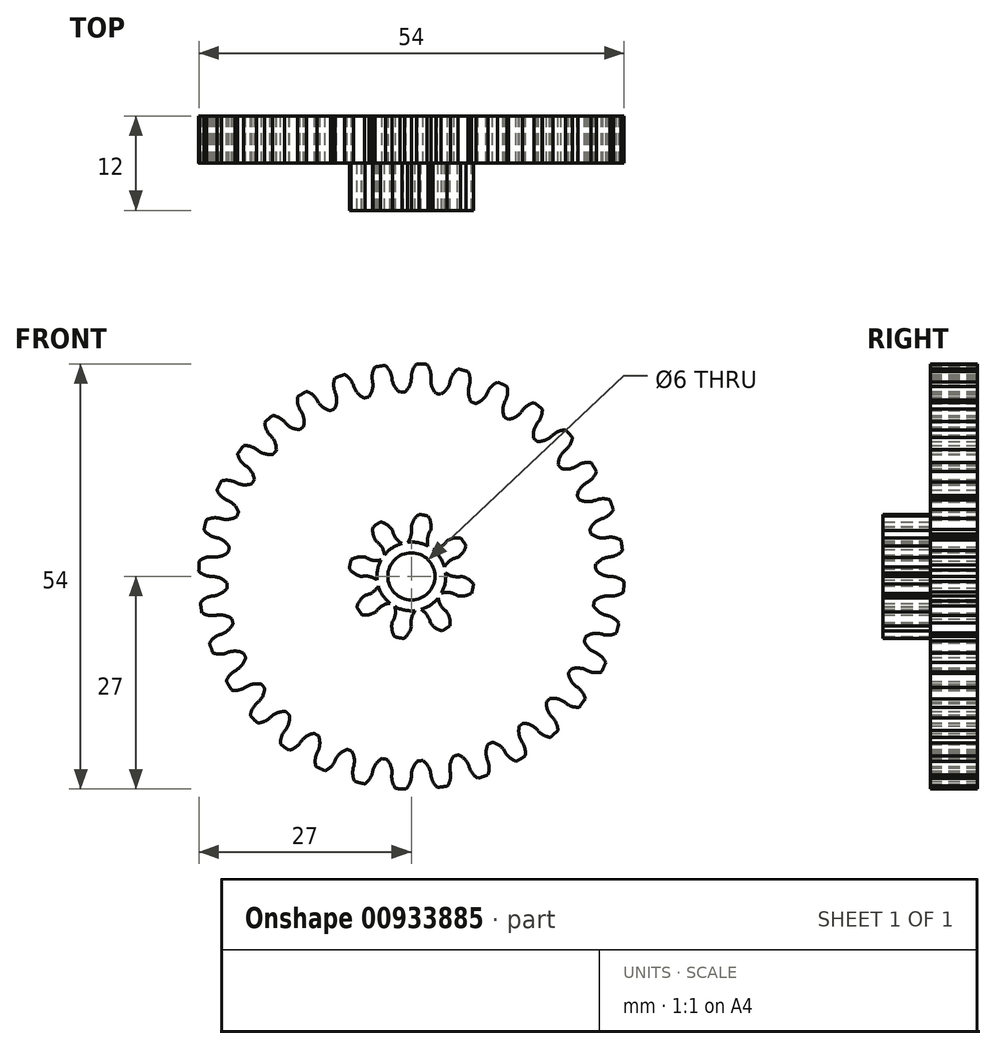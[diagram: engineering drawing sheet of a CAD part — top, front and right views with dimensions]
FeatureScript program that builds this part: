
annotation { "Feature Type Name" : "Feature", "Feature Type Description" : "" }
export const myFeature = defineFeature(function(context is Context, id is Id, definition is map)
    precondition{}
    {
        {
            var Q0;
            Q0=qCreatedBy(makeId("Front.planeOp"),FACE);
            var sketch = newSketch(context, id + "F0", { "sketchPlane" : qUnion([Q0])});
            skCircle(sketch, "E0", {"center": v(0, 0) * mm, "radius": 23.44 * mm});
            skArc(sketch, "E1", {"start": v(1.98, 26.94) * mm, "mid": v(1.33, 26.98) * mm, "end": v(0.67, 27) * mm});
            skArc(sketch, "E2", {"start": v(0.67, 27) * mm, "mid": v(0.2, 26.27) * mm, "end": v(0, 25.42) * mm});
            skArc(sketch, "E3", {"start": v(2.5, 25.3) * mm, "mid": v(2.58, 24.19) * mm, "end": v(3.14, 23.23) * mm});
            skArc(sketch, "E4", {"start": v(-0.85, 23.42) * mm, "mid": v(-0.2, 24.33) * mm, "end": v(0, 25.42) * mm});
            skArc(sketch, "E5.trimOffspring", {"start": v(2.5, 25.3) * mm, "mid": v(2.38, 26.17) * mm, "end": v(1.98, 26.94) * mm});
            skArc(sketch, "E6.1.0", {"start": v(-4.61, 26.62) * mm, "mid": v(-4.94, 25.8) * mm, "end": v(-4.96, 24.94) * mm});
            skArc(sketch, "E6.1.1", {"start": v(-2.49, 25.3) * mm, "mid": v(-2.19, 24.23) * mm, "end": v(-1.45, 23.4) * mm});
            skArc(sketch, "E6.1.2", {"start": v(-5.4, 22.8) * mm, "mid": v(-4.94, 23.82) * mm, "end": v(-4.96, 24.94) * mm});
            skArc(sketch, "E6.1.3", {"start": v(-2.49, 25.3) * mm, "mid": v(-2.77, 26.13) * mm, "end": v(-3.3, 26.8) * mm});
            skArc(sketch, "E6.1.4", {"start": v(-3.3, 26.8) * mm, "mid": v(-3.96, 26.72) * mm, "end": v(-4.61, 26.62) * mm});
            skArc(sketch, "E6.2.0", {"start": v(-9.72, 25.2) * mm, "mid": v(-9.88, 24.35) * mm, "end": v(-9.73, 23.49) * mm});
            skArc(sketch, "E6.2.1", {"start": v(-7.38, 24.33) * mm, "mid": v(-6.87, 23.34) * mm, "end": v(-5.98, 22.66) * mm});
            skArc(sketch, "E6.2.2", {"start": v(-9.75, 21.31) * mm, "mid": v(-9.49, 22.4) * mm, "end": v(-9.73, 23.49) * mm});
            skArc(sketch, "E6.2.3", {"start": v(-7.38, 24.33) * mm, "mid": v(-7.8, 25.09) * mm, "end": v(-8.48, 25.65) * mm});
            skArc(sketch, "E6.2.4", {"start": v(-8.48, 25.65) * mm, "mid": v(-9.1, 25.43) * mm, "end": v(-9.72, 25.2) * mm});
            skArc(sketch, "E6.3.0", {"start": v(-14.45, 22.82) * mm, "mid": v(-14.44, 21.95) * mm, "end": v(-14.12, 21.14) * mm});
            skArc(sketch, "E6.3.1", {"start": v(-11.98, 22.42) * mm, "mid": v(-11.3, 21.55) * mm, "end": v(-10.3, 21.06) * mm});
            skArc(sketch, "E6.3.2", {"start": v(-13.72, 19) * mm, "mid": v(-13.68, 20.12) * mm, "end": v(-14.12, 21.14) * mm});
            skArc(sketch, "E6.3.3", {"start": v(-11.98, 22.42) * mm, "mid": v(-12.55, 23.08) * mm, "end": v(-13.32, 23.5) * mm});
            skArc(sketch, "E6.3.4", {"start": v(-13.32, 23.5) * mm, "mid": v(-13.89, 23.17) * mm, "end": v(-14.45, 22.82) * mm});
            skArc(sketch, "E6.4.0", {"start": v(-18.62, 19.57) * mm, "mid": v(-18.44, 18.72) * mm, "end": v(-17.98, 17.98) * mm});
            skArc(sketch, "E6.4.1", {"start": v(-16.13, 19.65) * mm, "mid": v(-15.28, 18.93) * mm, "end": v(-14.2, 18.65) * mm});
            skArc(sketch, "E6.4.2", {"start": v(-17.16, 15.96) * mm, "mid": v(-17.34, 17.06) * mm, "end": v(-17.98, 17.98) * mm});
            skArc(sketch, "E6.4.3", {"start": v(-16.13, 19.65) * mm, "mid": v(-16.82, 20.19) * mm, "end": v(-17.65, 20.45) * mm});
            skArc(sketch, "E6.4.4", {"start": v(-17.65, 20.45) * mm, "mid": v(-18.14, 20.02) * mm, "end": v(-18.62, 19.57) * mm});
            skArc(sketch, "E6.5.0", {"start": v(-22.08, 15.56) * mm, "mid": v(-21.74, 14.76) * mm, "end": v(-21.14, 14.12) * mm});
            skArc(sketch, "E6.5.1", {"start": v(-19.65, 16.13) * mm, "mid": v(-18.68, 15.59) * mm, "end": v(-17.57, 15.52) * mm});
            skArc(sketch, "E6.5.2", {"start": v(-19.95, 12.3) * mm, "mid": v(-20.33, 13.35) * mm, "end": v(-21.14, 14.12) * mm});
            skArc(sketch, "E6.5.3", {"start": v(-19.65, 16.13) * mm, "mid": v(-20.43, 16.52) * mm, "end": v(-21.3, 16.62) * mm});
            skArc(sketch, "E6.5.4", {"start": v(-21.3, 16.62) * mm, "mid": v(-21.7, 16.1) * mm, "end": v(-22.08, 15.56) * mm});
            skArc(sketch, "E6.6.0", {"start": v(-24.7, 10.95) * mm, "mid": v(-24.2, 10.23) * mm, "end": v(-23.49, 9.73) * mm});
            skArc(sketch, "E6.6.1", {"start": v(-22.42, 11.99) * mm, "mid": v(-21.36, 11.64) * mm, "end": v(-20.26, 11.8) * mm});
            skArc(sketch, "E6.6.2", {"start": v(-21.96, 8.18) * mm, "mid": v(-22.55, 9.13) * mm, "end": v(-23.49, 9.73) * mm});
            skArc(sketch, "E6.6.3", {"start": v(-22.42, 11.99) * mm, "mid": v(-23.26, 12.22) * mm, "end": v(-24.13, 12.14) * mm});
            skArc(sketch, "E6.6.4", {"start": v(-24.13, 12.14) * mm, "mid": v(-24.42, 11.55) * mm, "end": v(-24.7, 10.95) * mm});
            skArc(sketch, "E6.7.0", {"start": v(-26.36, 5.92) * mm, "mid": v(-25.73, 5.32) * mm, "end": v(-24.94, 4.96) * mm});
            skArc(sketch, "E6.7.1", {"start": v(-24.33, 7.38) * mm, "mid": v(-23.22, 7.25) * mm, "end": v(-22.17, 7.61) * mm});
            skArc(sketch, "E6.7.2", {"start": v(-23.14, 3.74) * mm, "mid": v(-23.9, 4.55) * mm, "end": v(-24.94, 4.96) * mm});
            skArc(sketch, "E6.7.3", {"start": v(-24.33, 7.38) * mm, "mid": v(-25.2, 7.44) * mm, "end": v(-26.04, 7.2) * mm});
            skArc(sketch, "E6.7.4", {"start": v(-26.04, 7.2) * mm, "mid": v(-26.2, 6.56) * mm, "end": v(-26.36, 5.92) * mm});
            skArc(sketch, "E6.8.0", {"start": v(-27, 0.67) * mm, "mid": v(-26.27, 0.2) * mm, "end": v(-25.42, 0) * mm});
            skArc(sketch, "E6.8.1", {"start": v(-25.3, 2.5) * mm, "mid": v(-24.19, 2.58) * mm, "end": v(-23.23, 3.14) * mm});
            skArc(sketch, "E6.8.2", {"start": v(-23.42, -0.85) * mm, "mid": v(-24.33, -0.2) * mm, "end": v(-25.42, 0) * mm});
            skArc(sketch, "E6.8.3", {"start": v(-25.3, 2.5) * mm, "mid": v(-26.17, 2.38) * mm, "end": v(-26.94, 1.98) * mm});
            skArc(sketch, "E6.8.4", {"start": v(-26.94, 1.98) * mm, "mid": v(-26.98, 1.33) * mm, "end": v(-27, 0.67) * mm});
            skArc(sketch, "E6.9.0", {"start": v(-26.62, -4.61) * mm, "mid": v(-25.8, -4.94) * mm, "end": v(-24.94, -4.96) * mm});
            skArc(sketch, "E6.9.1", {"start": v(-25.3, -2.49) * mm, "mid": v(-24.23, -2.19) * mm, "end": v(-23.4, -1.45) * mm});
            skArc(sketch, "E6.9.2", {"start": v(-22.8, -5.4) * mm, "mid": v(-23.82, -4.94) * mm, "end": v(-24.94, -4.96) * mm});
            skArc(sketch, "E6.9.3", {"start": v(-25.3, -2.49) * mm, "mid": v(-26.13, -2.77) * mm, "end": v(-26.8, -3.3) * mm});
            skArc(sketch, "E6.9.4", {"start": v(-26.8, -3.3) * mm, "mid": v(-26.72, -3.96) * mm, "end": v(-26.62, -4.61) * mm});
            skArc(sketch, "E6.10.0", {"start": v(-25.2, -9.72) * mm, "mid": v(-24.35, -9.88) * mm, "end": v(-23.49, -9.73) * mm});
            skArc(sketch, "E6.10.1", {"start": v(-24.33, -7.38) * mm, "mid": v(-23.34, -6.87) * mm, "end": v(-22.66, -5.98) * mm});
            skArc(sketch, "E6.10.2", {"start": v(-21.31, -9.75) * mm, "mid": v(-22.4, -9.49) * mm, "end": v(-23.49, -9.73) * mm});
            skArc(sketch, "E6.10.3", {"start": v(-24.33, -7.38) * mm, "mid": v(-25.09, -7.8) * mm, "end": v(-25.65, -8.48) * mm});
            skArc(sketch, "E6.10.4", {"start": v(-25.65, -8.48) * mm, "mid": v(-25.43, -9.1) * mm, "end": v(-25.2, -9.72) * mm});
            skArc(sketch, "E6.11.0", {"start": v(-22.82, -14.45) * mm, "mid": v(-21.95, -14.44) * mm, "end": v(-21.14, -14.12) * mm});
            skArc(sketch, "E6.11.1", {"start": v(-22.42, -11.98) * mm, "mid": v(-21.55, -11.3) * mm, "end": v(-21.06, -10.3) * mm});
            skArc(sketch, "E6.11.2", {"start": v(-19, -13.72) * mm, "mid": v(-20.12, -13.68) * mm, "end": v(-21.14, -14.12) * mm});
            skArc(sketch, "E6.11.3", {"start": v(-22.42, -11.98) * mm, "mid": v(-23.08, -12.55) * mm, "end": v(-23.5, -13.32) * mm});
            skArc(sketch, "E6.11.4", {"start": v(-23.5, -13.32) * mm, "mid": v(-23.17, -13.89) * mm, "end": v(-22.82, -14.45) * mm});
            skArc(sketch, "E6.12.0", {"start": v(-19.57, -18.62) * mm, "mid": v(-18.72, -18.44) * mm, "end": v(-17.98, -17.98) * mm});
            skArc(sketch, "E6.12.1", {"start": v(-19.65, -16.13) * mm, "mid": v(-18.93, -15.28) * mm, "end": v(-18.65, -14.2) * mm});
            skArc(sketch, "E6.12.2", {"start": v(-15.96, -17.16) * mm, "mid": v(-17.06, -17.34) * mm, "end": v(-17.98, -17.98) * mm});
            skArc(sketch, "E6.12.3", {"start": v(-19.65, -16.13) * mm, "mid": v(-20.19, -16.82) * mm, "end": v(-20.45, -17.65) * mm});
            skArc(sketch, "E6.12.4", {"start": v(-20.45, -17.65) * mm, "mid": v(-20.02, -18.14) * mm, "end": v(-19.57, -18.62) * mm});
            skArc(sketch, "E6.13.0", {"start": v(-15.56, -22.08) * mm, "mid": v(-14.76, -21.74) * mm, "end": v(-14.12, -21.14) * mm});
            skArc(sketch, "E6.13.1", {"start": v(-16.13, -19.65) * mm, "mid": v(-15.59, -18.68) * mm, "end": v(-15.52, -17.57) * mm});
            skArc(sketch, "E6.13.2", {"start": v(-12.3, -19.95) * mm, "mid": v(-13.35, -20.33) * mm, "end": v(-14.12, -21.14) * mm});
            skArc(sketch, "E6.13.3", {"start": v(-16.13, -19.65) * mm, "mid": v(-16.52, -20.43) * mm, "end": v(-16.62, -21.3) * mm});
            skArc(sketch, "E6.13.4", {"start": v(-16.62, -21.3) * mm, "mid": v(-16.1, -21.7) * mm, "end": v(-15.56, -22.08) * mm});
            skArc(sketch, "E6.14.0", {"start": v(-10.95, -24.7) * mm, "mid": v(-10.23, -24.2) * mm, "end": v(-9.73, -23.49) * mm});
            skArc(sketch, "E6.14.1", {"start": v(-11.99, -22.42) * mm, "mid": v(-11.64, -21.36) * mm, "end": v(-11.8, -20.26) * mm});
            skArc(sketch, "E6.14.2", {"start": v(-8.18, -21.96) * mm, "mid": v(-9.13, -22.55) * mm, "end": v(-9.73, -23.49) * mm});
            skArc(sketch, "E6.14.3", {"start": v(-11.99, -22.42) * mm, "mid": v(-12.22, -23.26) * mm, "end": v(-12.14, -24.13) * mm});
            skArc(sketch, "E6.14.4", {"start": v(-12.14, -24.13) * mm, "mid": v(-11.55, -24.42) * mm, "end": v(-10.95, -24.7) * mm});
            skArc(sketch, "E6.15.0", {"start": v(-5.92, -26.36) * mm, "mid": v(-5.32, -25.73) * mm, "end": v(-4.96, -24.94) * mm});
            skArc(sketch, "E6.15.1", {"start": v(-7.38, -24.33) * mm, "mid": v(-7.25, -23.22) * mm, "end": v(-7.61, -22.17) * mm});
            skArc(sketch, "E6.15.2", {"start": v(-3.74, -23.14) * mm, "mid": v(-4.55, -23.9) * mm, "end": v(-4.96, -24.94) * mm});
            skArc(sketch, "E6.15.3", {"start": v(-7.38, -24.33) * mm, "mid": v(-7.44, -25.2) * mm, "end": v(-7.2, -26.04) * mm});
            skArc(sketch, "E6.15.4", {"start": v(-7.2, -26.04) * mm, "mid": v(-6.56, -26.2) * mm, "end": v(-5.92, -26.36) * mm});
            skArc(sketch, "E6.16.0", {"start": v(-0.67, -27) * mm, "mid": v(-0.2, -26.27) * mm, "end": v(0, -25.42) * mm});
            skArc(sketch, "E6.16.1", {"start": v(-2.5, -25.3) * mm, "mid": v(-2.58, -24.19) * mm, "end": v(-3.14, -23.23) * mm});
            skArc(sketch, "E6.16.2", {"start": v(0.85, -23.42) * mm, "mid": v(0.2, -24.33) * mm, "end": v(0, -25.42) * mm});
            skArc(sketch, "E6.16.3", {"start": v(-2.5, -25.3) * mm, "mid": v(-2.38, -26.17) * mm, "end": v(-1.98, -26.94) * mm});
            skArc(sketch, "E6.16.4", {"start": v(-1.98, -26.94) * mm, "mid": v(-1.33, -26.98) * mm, "end": v(-0.67, -27) * mm});
            skArc(sketch, "E6.17.0", {"start": v(4.61, -26.62) * mm, "mid": v(4.94, -25.8) * mm, "end": v(4.96, -24.94) * mm});
            skArc(sketch, "E6.17.1", {"start": v(2.49, -25.3) * mm, "mid": v(2.19, -24.23) * mm, "end": v(1.45, -23.4) * mm});
            skArc(sketch, "E6.17.2", {"start": v(5.4, -22.8) * mm, "mid": v(4.94, -23.82) * mm, "end": v(4.96, -24.94) * mm});
            skArc(sketch, "E6.17.3", {"start": v(2.49, -25.3) * mm, "mid": v(2.77, -26.13) * mm, "end": v(3.3, -26.8) * mm});
            skArc(sketch, "E6.17.4", {"start": v(3.3, -26.8) * mm, "mid": v(3.96, -26.72) * mm, "end": v(4.61, -26.62) * mm});
            skArc(sketch, "E6.18.0", {"start": v(9.72, -25.2) * mm, "mid": v(9.88, -24.35) * mm, "end": v(9.73, -23.49) * mm});
            skArc(sketch, "E6.18.1", {"start": v(7.38, -24.33) * mm, "mid": v(6.87, -23.34) * mm, "end": v(5.98, -22.66) * mm});
            skArc(sketch, "E6.18.2", {"start": v(9.75, -21.31) * mm, "mid": v(9.49, -22.4) * mm, "end": v(9.73, -23.49) * mm});
            skArc(sketch, "E6.18.3", {"start": v(7.38, -24.33) * mm, "mid": v(7.8, -25.09) * mm, "end": v(8.48, -25.65) * mm});
            skArc(sketch, "E6.18.4", {"start": v(8.48, -25.65) * mm, "mid": v(9.1, -25.43) * mm, "end": v(9.72, -25.2) * mm});
            skArc(sketch, "E6.19.0", {"start": v(14.45, -22.82) * mm, "mid": v(14.44, -21.95) * mm, "end": v(14.12, -21.14) * mm});
            skArc(sketch, "E6.19.1", {"start": v(11.98, -22.42) * mm, "mid": v(11.3, -21.55) * mm, "end": v(10.3, -21.06) * mm});
            skArc(sketch, "E6.19.2", {"start": v(13.72, -19) * mm, "mid": v(13.68, -20.12) * mm, "end": v(14.12, -21.14) * mm});
            skArc(sketch, "E6.19.3", {"start": v(11.98, -22.42) * mm, "mid": v(12.55, -23.08) * mm, "end": v(13.32, -23.5) * mm});
            skArc(sketch, "E6.19.4", {"start": v(13.32, -23.5) * mm, "mid": v(13.89, -23.17) * mm, "end": v(14.45, -22.82) * mm});
            skArc(sketch, "E6.20.0", {"start": v(18.62, -19.57) * mm, "mid": v(18.44, -18.72) * mm, "end": v(17.98, -17.98) * mm});
            skArc(sketch, "E6.20.1", {"start": v(16.13, -19.65) * mm, "mid": v(15.28, -18.93) * mm, "end": v(14.2, -18.65) * mm});
            skArc(sketch, "E6.20.2", {"start": v(17.16, -15.96) * mm, "mid": v(17.34, -17.06) * mm, "end": v(17.98, -17.98) * mm});
            skArc(sketch, "E6.20.3", {"start": v(16.13, -19.65) * mm, "mid": v(16.82, -20.19) * mm, "end": v(17.65, -20.45) * mm});
            skArc(sketch, "E6.20.4", {"start": v(17.65, -20.45) * mm, "mid": v(18.14, -20.02) * mm, "end": v(18.62, -19.57) * mm});
            skArc(sketch, "E6.21.0", {"start": v(22.08, -15.56) * mm, "mid": v(21.74, -14.76) * mm, "end": v(21.14, -14.12) * mm});
            skArc(sketch, "E6.21.1", {"start": v(19.65, -16.13) * mm, "mid": v(18.68, -15.59) * mm, "end": v(17.57, -15.52) * mm});
            skArc(sketch, "E6.21.2", {"start": v(19.95, -12.3) * mm, "mid": v(20.33, -13.35) * mm, "end": v(21.14, -14.12) * mm});
            skArc(sketch, "E6.21.3", {"start": v(19.65, -16.13) * mm, "mid": v(20.43, -16.52) * mm, "end": v(21.3, -16.62) * mm});
            skArc(sketch, "E6.21.4", {"start": v(21.3, -16.62) * mm, "mid": v(21.7, -16.1) * mm, "end": v(22.08, -15.56) * mm});
            skArc(sketch, "E6.22.0", {"start": v(24.7, -10.95) * mm, "mid": v(24.2, -10.23) * mm, "end": v(23.49, -9.73) * mm});
            skArc(sketch, "E6.22.1", {"start": v(22.42, -11.99) * mm, "mid": v(21.36, -11.64) * mm, "end": v(20.26, -11.8) * mm});
            skArc(sketch, "E6.22.2", {"start": v(21.96, -8.18) * mm, "mid": v(22.55, -9.13) * mm, "end": v(23.49, -9.73) * mm});
            skArc(sketch, "E6.22.3", {"start": v(22.42, -11.99) * mm, "mid": v(23.26, -12.22) * mm, "end": v(24.13, -12.14) * mm});
            skArc(sketch, "E6.22.4", {"start": v(24.13, -12.14) * mm, "mid": v(24.42, -11.55) * mm, "end": v(24.7, -10.95) * mm});
            skArc(sketch, "E6.23.0", {"start": v(26.36, -5.92) * mm, "mid": v(25.73, -5.32) * mm, "end": v(24.94, -4.96) * mm});
            skArc(sketch, "E6.23.1", {"start": v(24.33, -7.38) * mm, "mid": v(23.22, -7.25) * mm, "end": v(22.17, -7.61) * mm});
            skArc(sketch, "E6.23.2", {"start": v(23.14, -3.74) * mm, "mid": v(23.9, -4.55) * mm, "end": v(24.94, -4.96) * mm});
            skArc(sketch, "E6.23.3", {"start": v(24.33, -7.38) * mm, "mid": v(25.2, -7.44) * mm, "end": v(26.04, -7.2) * mm});
            skArc(sketch, "E6.23.4", {"start": v(26.04, -7.2) * mm, "mid": v(26.2, -6.56) * mm, "end": v(26.36, -5.92) * mm});
            skArc(sketch, "E6.24.0", {"start": v(27, -0.67) * mm, "mid": v(26.27, -0.2) * mm, "end": v(25.42, 0) * mm});
            skArc(sketch, "E6.24.1", {"start": v(25.3, -2.5) * mm, "mid": v(24.19, -2.58) * mm, "end": v(23.23, -3.14) * mm});
            skArc(sketch, "E6.24.2", {"start": v(23.42, 0.85) * mm, "mid": v(24.33, 0.2) * mm, "end": v(25.42, 0) * mm});
            skArc(sketch, "E6.24.3", {"start": v(25.3, -2.5) * mm, "mid": v(26.17, -2.38) * mm, "end": v(26.94, -1.98) * mm});
            skArc(sketch, "E6.24.4", {"start": v(26.94, -1.98) * mm, "mid": v(26.98, -1.33) * mm, "end": v(27, -0.67) * mm});
            skArc(sketch, "E6.25.0", {"start": v(26.62, 4.61) * mm, "mid": v(25.8, 4.94) * mm, "end": v(24.94, 4.96) * mm});
            skArc(sketch, "E6.25.1", {"start": v(25.3, 2.49) * mm, "mid": v(24.23, 2.19) * mm, "end": v(23.4, 1.45) * mm});
            skArc(sketch, "E6.25.2", {"start": v(22.8, 5.4) * mm, "mid": v(23.82, 4.94) * mm, "end": v(24.94, 4.96) * mm});
            skArc(sketch, "E6.25.3", {"start": v(25.3, 2.49) * mm, "mid": v(26.13, 2.77) * mm, "end": v(26.8, 3.3) * mm});
            skArc(sketch, "E6.25.4", {"start": v(26.8, 3.3) * mm, "mid": v(26.72, 3.96) * mm, "end": v(26.62, 4.61) * mm});
            skArc(sketch, "E6.26.0", {"start": v(25.2, 9.72) * mm, "mid": v(24.35, 9.88) * mm, "end": v(23.49, 9.73) * mm});
            skArc(sketch, "E6.26.1", {"start": v(24.33, 7.38) * mm, "mid": v(23.34, 6.87) * mm, "end": v(22.66, 5.98) * mm});
            skArc(sketch, "E6.26.2", {"start": v(21.31, 9.75) * mm, "mid": v(22.4, 9.49) * mm, "end": v(23.49, 9.73) * mm});
            skArc(sketch, "E6.26.3", {"start": v(24.33, 7.38) * mm, "mid": v(25.09, 7.8) * mm, "end": v(25.65, 8.48) * mm});
            skArc(sketch, "E6.26.4", {"start": v(25.65, 8.48) * mm, "mid": v(25.43, 9.1) * mm, "end": v(25.2, 9.72) * mm});
            skArc(sketch, "E6.27.0", {"start": v(22.82, 14.45) * mm, "mid": v(21.95, 14.44) * mm, "end": v(21.14, 14.12) * mm});
            skArc(sketch, "E6.27.1", {"start": v(22.42, 11.98) * mm, "mid": v(21.55, 11.3) * mm, "end": v(21.06, 10.3) * mm});
            skArc(sketch, "E6.27.2", {"start": v(19, 13.72) * mm, "mid": v(20.12, 13.68) * mm, "end": v(21.14, 14.12) * mm});
            skArc(sketch, "E6.27.3", {"start": v(22.42, 11.98) * mm, "mid": v(23.08, 12.55) * mm, "end": v(23.5, 13.32) * mm});
            skArc(sketch, "E6.27.4", {"start": v(23.5, 13.32) * mm, "mid": v(23.17, 13.89) * mm, "end": v(22.82, 14.45) * mm});
            skArc(sketch, "E6.28.0", {"start": v(19.57, 18.62) * mm, "mid": v(18.72, 18.44) * mm, "end": v(17.98, 17.98) * mm});
            skArc(sketch, "E6.28.1", {"start": v(19.65, 16.13) * mm, "mid": v(18.93, 15.28) * mm, "end": v(18.65, 14.2) * mm});
            skArc(sketch, "E6.28.2", {"start": v(15.96, 17.16) * mm, "mid": v(17.06, 17.34) * mm, "end": v(17.98, 17.98) * mm});
            skArc(sketch, "E6.28.3", {"start": v(19.65, 16.13) * mm, "mid": v(20.19, 16.82) * mm, "end": v(20.45, 17.65) * mm});
            skArc(sketch, "E6.28.4", {"start": v(20.45, 17.65) * mm, "mid": v(20.02, 18.14) * mm, "end": v(19.57, 18.62) * mm});
            skArc(sketch, "E6.29.0", {"start": v(15.56, 22.08) * mm, "mid": v(14.76, 21.74) * mm, "end": v(14.12, 21.14) * mm});
            skArc(sketch, "E6.29.1", {"start": v(16.13, 19.65) * mm, "mid": v(15.59, 18.68) * mm, "end": v(15.52, 17.57) * mm});
            skArc(sketch, "E6.29.2", {"start": v(12.3, 19.95) * mm, "mid": v(13.35, 20.33) * mm, "end": v(14.12, 21.14) * mm});
            skArc(sketch, "E6.29.3", {"start": v(16.13, 19.65) * mm, "mid": v(16.52, 20.43) * mm, "end": v(16.62, 21.3) * mm});
            skArc(sketch, "E6.29.4", {"start": v(16.62, 21.3) * mm, "mid": v(16.1, 21.7) * mm, "end": v(15.56, 22.08) * mm});
            skArc(sketch, "E6.30.0", {"start": v(10.95, 24.7) * mm, "mid": v(10.23, 24.2) * mm, "end": v(9.73, 23.49) * mm});
            skArc(sketch, "E6.30.1", {"start": v(11.99, 22.42) * mm, "mid": v(11.64, 21.36) * mm, "end": v(11.8, 20.26) * mm});
            skArc(sketch, "E6.30.2", {"start": v(8.18, 21.96) * mm, "mid": v(9.13, 22.55) * mm, "end": v(9.73, 23.49) * mm});
            skArc(sketch, "E6.30.3", {"start": v(11.99, 22.42) * mm, "mid": v(12.22, 23.26) * mm, "end": v(12.14, 24.13) * mm});
            skArc(sketch, "E6.30.4", {"start": v(12.14, 24.13) * mm, "mid": v(11.55, 24.42) * mm, "end": v(10.95, 24.7) * mm});
            skArc(sketch, "E6.31.0", {"start": v(5.92, 26.36) * mm, "mid": v(5.32, 25.73) * mm, "end": v(4.96, 24.94) * mm});
            skArc(sketch, "E6.31.1", {"start": v(7.38, 24.33) * mm, "mid": v(7.25, 23.22) * mm, "end": v(7.61, 22.17) * mm});
            skArc(sketch, "E6.31.2", {"start": v(3.74, 23.14) * mm, "mid": v(4.55, 23.9) * mm, "end": v(4.96, 24.94) * mm});
            skArc(sketch, "E6.31.3", {"start": v(7.38, 24.33) * mm, "mid": v(7.44, 25.2) * mm, "end": v(7.2, 26.04) * mm});
            skArc(sketch, "E6.31.4", {"start": v(7.2, 26.04) * mm, "mid": v(6.56, 26.2) * mm, "end": v(5.92, 26.36) * mm});
            skSolve(sketch);
        }
        {
            var Q0;
            Q0 = qSketchRegion(id + "F0", true);
            extrude(context, id + "F1", {"entities" : qUnion([Q0]), "depth" : 6 * mm, "offsetDistance" : 25 * mm});
        }
        {
            var Q0;
            Q0=makeQuery(id+"F1.opExtrude","CAP_FACE",FACE,{"disambiguationData":[OSD([sQuery(id+"F0.wireOp",EDGE,"E0"),sQuery(id+"F0.wireOp",EDGE,"E1"),sQuery(id+"F0.wireOp",EDGE,"E2"),sQuery(id+"F0.wireOp",EDGE,"E3"),sQuery(id+"F0.wireOp",EDGE,"E4"),sQuery(id+"F0.wireOp",EDGE,"E5.trimOffspring"),sQuery(id+"F0.wireOp",EDGE,"E6.1.0"),sQuery(id+"F0.wireOp",EDGE,"E6.1.1"),sQuery(id+"F0.wireOp",EDGE,"E6.1.2"),sQuery(id+"F0.wireOp",EDGE,"E6.1.3"),sQuery(id+"F0.wireOp",EDGE,"E6.1.4"),sQuery(id+"F0.wireOp",EDGE,"E6.2.0"),sQuery(id+"F0.wireOp",EDGE,"E6.2.1"),sQuery(id+"F0.wireOp",EDGE,"E6.2.2"),sQuery(id+"F0.wireOp",EDGE,"E6.2.3"),sQuery(id+"F0.wireOp",EDGE,"E6.2.4"),sQuery(id+"F0.wireOp",EDGE,"E6.3.0"),sQuery(id+"F0.wireOp",EDGE,"E6.3.1"),sQuery(id+"F0.wireOp",EDGE,"E6.3.2"),sQuery(id+"F0.wireOp",EDGE,"E6.3.3"),sQuery(id+"F0.wireOp",EDGE,"E6.3.4"),sQuery(id+"F0.wireOp",EDGE,"E6.4.0"),sQuery(id+"F0.wireOp",EDGE,"E6.4.1"),sQuery(id+"F0.wireOp",EDGE,"E6.4.2"),sQuery(id+"F0.wireOp",EDGE,"E6.4.3"),sQuery(id+"F0.wireOp",EDGE,"E6.4.4"),sQuery(id+"F0.wireOp",EDGE,"E6.5.0"),sQuery(id+"F0.wireOp",EDGE,"E6.5.1"),sQuery(id+"F0.wireOp",EDGE,"E6.5.2"),sQuery(id+"F0.wireOp",EDGE,"E6.5.3"),sQuery(id+"F0.wireOp",EDGE,"E6.5.4"),sQuery(id+"F0.wireOp",EDGE,"E6.6.0"),sQuery(id+"F0.wireOp",EDGE,"E6.6.1"),sQuery(id+"F0.wireOp",EDGE,"E6.6.2"),sQuery(id+"F0.wireOp",EDGE,"E6.6.3"),sQuery(id+"F0.wireOp",EDGE,"E6.6.4"),sQuery(id+"F0.wireOp",EDGE,"E6.7.0"),sQuery(id+"F0.wireOp",EDGE,"E6.7.1"),sQuery(id+"F0.wireOp",EDGE,"E6.7.2"),sQuery(id+"F0.wireOp",EDGE,"E6.7.3"),sQuery(id+"F0.wireOp",EDGE,"E6.7.4"),sQuery(id+"F0.wireOp",EDGE,"E6.8.0"),sQuery(id+"F0.wireOp",EDGE,"E6.8.1"),sQuery(id+"F0.wireOp",EDGE,"E6.8.2"),sQuery(id+"F0.wireOp",EDGE,"E6.8.3"),sQuery(id+"F0.wireOp",EDGE,"E6.8.4"),sQuery(id+"F0.wireOp",EDGE,"E6.9.0"),sQuery(id+"F0.wireOp",EDGE,"E6.9.1"),sQuery(id+"F0.wireOp",EDGE,"E6.9.2"),sQuery(id+"F0.wireOp",EDGE,"E6.9.3"),sQuery(id+"F0.wireOp",EDGE,"E6.9.4"),sQuery(id+"F0.wireOp",EDGE,"E6.10.0"),sQuery(id+"F0.wireOp",EDGE,"E6.10.1"),sQuery(id+"F0.wireOp",EDGE,"E6.10.2"),sQuery(id+"F0.wireOp",EDGE,"E6.10.3"),sQuery(id+"F0.wireOp",EDGE,"E6.10.4"),sQuery(id+"F0.wireOp",EDGE,"E6.11.0"),sQuery(id+"F0.wireOp",EDGE,"E6.11.1"),sQuery(id+"F0.wireOp",EDGE,"E6.11.2"),sQuery(id+"F0.wireOp",EDGE,"E6.11.3"),sQuery(id+"F0.wireOp",EDGE,"E6.11.4"),sQuery(id+"F0.wireOp",EDGE,"E6.12.0"),sQuery(id+"F0.wireOp",EDGE,"E6.12.1"),sQuery(id+"F0.wireOp",EDGE,"E6.12.2"),sQuery(id+"F0.wireOp",EDGE,"E6.12.3"),sQuery(id+"F0.wireOp",EDGE,"E6.12.4"),sQuery(id+"F0.wireOp",EDGE,"E6.13.0"),sQuery(id+"F0.wireOp",EDGE,"E6.13.1"),sQuery(id+"F0.wireOp",EDGE,"E6.13.2"),sQuery(id+"F0.wireOp",EDGE,"E6.13.3"),sQuery(id+"F0.wireOp",EDGE,"E6.13.4"),sQuery(id+"F0.wireOp",EDGE,"E6.14.0"),sQuery(id+"F0.wireOp",EDGE,"E6.14.1"),sQuery(id+"F0.wireOp",EDGE,"E6.14.2"),sQuery(id+"F0.wireOp",EDGE,"E6.14.3"),sQuery(id+"F0.wireOp",EDGE,"E6.14.4"),sQuery(id+"F0.wireOp",EDGE,"E6.15.0"),sQuery(id+"F0.wireOp",EDGE,"E6.15.1"),sQuery(id+"F0.wireOp",EDGE,"E6.15.2"),sQuery(id+"F0.wireOp",EDGE,"E6.15.3"),sQuery(id+"F0.wireOp",EDGE,"E6.15.4"),sQuery(id+"F0.wireOp",EDGE,"E6.16.0"),sQuery(id+"F0.wireOp",EDGE,"E6.16.1"),sQuery(id+"F0.wireOp",EDGE,"E6.16.2"),sQuery(id+"F0.wireOp",EDGE,"E6.16.3"),sQuery(id+"F0.wireOp",EDGE,"E6.16.4"),sQuery(id+"F0.wireOp",EDGE,"E6.17.0"),sQuery(id+"F0.wireOp",EDGE,"E6.17.1"),sQuery(id+"F0.wireOp",EDGE,"E6.17.2"),sQuery(id+"F0.wireOp",EDGE,"E6.17.3"),sQuery(id+"F0.wireOp",EDGE,"E6.17.4"),sQuery(id+"F0.wireOp",EDGE,"E6.18.0"),sQuery(id+"F0.wireOp",EDGE,"E6.18.1"),sQuery(id+"F0.wireOp",EDGE,"E6.18.2"),sQuery(id+"F0.wireOp",EDGE,"E6.18.3"),sQuery(id+"F0.wireOp",EDGE,"E6.18.4"),sQuery(id+"F0.wireOp",EDGE,"E6.19.0"),sQuery(id+"F0.wireOp",EDGE,"E6.19.1"),sQuery(id+"F0.wireOp",EDGE,"E6.19.2"),sQuery(id+"F0.wireOp",EDGE,"E6.19.3"),sQuery(id+"F0.wireOp",EDGE,"E6.19.4"),sQuery(id+"F0.wireOp",EDGE,"E6.20.0"),sQuery(id+"F0.wireOp",EDGE,"E6.20.1"),sQuery(id+"F0.wireOp",EDGE,"E6.20.2"),sQuery(id+"F0.wireOp",EDGE,"E6.20.3"),sQuery(id+"F0.wireOp",EDGE,"E6.20.4"),sQuery(id+"F0.wireOp",EDGE,"E6.21.0"),sQuery(id+"F0.wireOp",EDGE,"E6.21.1"),sQuery(id+"F0.wireOp",EDGE,"E6.21.2"),sQuery(id+"F0.wireOp",EDGE,"E6.21.3"),sQuery(id+"F0.wireOp",EDGE,"E6.21.4"),sQuery(id+"F0.wireOp",EDGE,"E6.22.0"),sQuery(id+"F0.wireOp",EDGE,"E6.22.1"),sQuery(id+"F0.wireOp",EDGE,"E6.22.2"),sQuery(id+"F0.wireOp",EDGE,"E6.22.3"),sQuery(id+"F0.wireOp",EDGE,"E6.22.4"),sQuery(id+"F0.wireOp",EDGE,"E6.23.0"),sQuery(id+"F0.wireOp",EDGE,"E6.23.1"),sQuery(id+"F0.wireOp",EDGE,"E6.23.2"),sQuery(id+"F0.wireOp",EDGE,"E6.23.3"),sQuery(id+"F0.wireOp",EDGE,"E6.23.4"),sQuery(id+"F0.wireOp",EDGE,"E6.24.0"),sQuery(id+"F0.wireOp",EDGE,"E6.24.1"),sQuery(id+"F0.wireOp",EDGE,"E6.24.2"),sQuery(id+"F0.wireOp",EDGE,"E6.24.3"),sQuery(id+"F0.wireOp",EDGE,"E6.24.4"),sQuery(id+"F0.wireOp",EDGE,"E6.25.0"),sQuery(id+"F0.wireOp",EDGE,"E6.25.1"),sQuery(id+"F0.wireOp",EDGE,"E6.25.2"),sQuery(id+"F0.wireOp",EDGE,"E6.25.3"),sQuery(id+"F0.wireOp",EDGE,"E6.25.4"),sQuery(id+"F0.wireOp",EDGE,"E6.26.0"),sQuery(id+"F0.wireOp",EDGE,"E6.26.1"),sQuery(id+"F0.wireOp",EDGE,"E6.26.2"),sQuery(id+"F0.wireOp",EDGE,"E6.26.3"),sQuery(id+"F0.wireOp",EDGE,"E6.26.4"),sQuery(id+"F0.wireOp",EDGE,"E6.27.0"),sQuery(id+"F0.wireOp",EDGE,"E6.27.1"),sQuery(id+"F0.wireOp",EDGE,"E6.27.2"),sQuery(id+"F0.wireOp",EDGE,"E6.27.3"),sQuery(id+"F0.wireOp",EDGE,"E6.27.4"),sQuery(id+"F0.wireOp",EDGE,"E6.28.0"),sQuery(id+"F0.wireOp",EDGE,"E6.28.1"),sQuery(id+"F0.wireOp",EDGE,"E6.28.2"),sQuery(id+"F0.wireOp",EDGE,"E6.28.3"),sQuery(id+"F0.wireOp",EDGE,"E6.28.4"),sQuery(id+"F0.wireOp",EDGE,"E6.29.0"),sQuery(id+"F0.wireOp",EDGE,"E6.29.1"),sQuery(id+"F0.wireOp",EDGE,"E6.29.2"),sQuery(id+"F0.wireOp",EDGE,"E6.29.3"),sQuery(id+"F0.wireOp",EDGE,"E6.29.4"),sQuery(id+"F0.wireOp",EDGE,"E6.30.0"),sQuery(id+"F0.wireOp",EDGE,"E6.30.1"),sQuery(id+"F0.wireOp",EDGE,"E6.30.2"),sQuery(id+"F0.wireOp",EDGE,"E6.30.3"),sQuery(id+"F0.wireOp",EDGE,"E6.30.4"),sQuery(id+"F0.wireOp",EDGE,"E6.31.0"),sQuery(id+"F0.wireOp",EDGE,"E6.31.1"),sQuery(id+"F0.wireOp",EDGE,"E6.31.2"),sQuery(id+"F0.wireOp",EDGE,"E6.31.3"),sQuery(id+"F0.wireOp",EDGE,"E6.31.4")])],"isStart":false});
            var sketch = newSketch(context, id + "F2", { "sketchPlane" : qUnion([Q0])});
            skCircle(sketch, "E7", {"center": v(0, 0) * mm, "radius": 3 * mm});
            skSolve(sketch);
        }
        {
            var Q0;
            Q0 = qSketchRegion(id + "F2", true);
            extrude(context, id + "F3", {"entities" : qUnion([Q0]), "operationType" : NewBodyOperationType.REMOVE, "endBound" : BoundingType.THROUGH_ALL, "oppositeDirection" : true, "depth" : 25 * mm, "offsetDistance" : 25 * mm});
        }
        {
            var Q0;
            Q0=makeQuery(id+"F1.opExtrude","CAP_FACE",FACE,{"disambiguationData":[OSD([sQuery(id+"F0.wireOp",EDGE,"E0"),sQuery(id+"F0.wireOp",EDGE,"E1"),sQuery(id+"F0.wireOp",EDGE,"E2"),sQuery(id+"F0.wireOp",EDGE,"E3"),sQuery(id+"F0.wireOp",EDGE,"E4"),sQuery(id+"F0.wireOp",EDGE,"E5.trimOffspring"),sQuery(id+"F0.wireOp",EDGE,"E6.1.0"),sQuery(id+"F0.wireOp",EDGE,"E6.1.1"),sQuery(id+"F0.wireOp",EDGE,"E6.1.2"),sQuery(id+"F0.wireOp",EDGE,"E6.1.3"),sQuery(id+"F0.wireOp",EDGE,"E6.1.4"),sQuery(id+"F0.wireOp",EDGE,"E6.2.0"),sQuery(id+"F0.wireOp",EDGE,"E6.2.1"),sQuery(id+"F0.wireOp",EDGE,"E6.2.2"),sQuery(id+"F0.wireOp",EDGE,"E6.2.3"),sQuery(id+"F0.wireOp",EDGE,"E6.2.4"),sQuery(id+"F0.wireOp",EDGE,"E6.3.0"),sQuery(id+"F0.wireOp",EDGE,"E6.3.1"),sQuery(id+"F0.wireOp",EDGE,"E6.3.2"),sQuery(id+"F0.wireOp",EDGE,"E6.3.3"),sQuery(id+"F0.wireOp",EDGE,"E6.3.4"),sQuery(id+"F0.wireOp",EDGE,"E6.4.0"),sQuery(id+"F0.wireOp",EDGE,"E6.4.1"),sQuery(id+"F0.wireOp",EDGE,"E6.4.2"),sQuery(id+"F0.wireOp",EDGE,"E6.4.3"),sQuery(id+"F0.wireOp",EDGE,"E6.4.4"),sQuery(id+"F0.wireOp",EDGE,"E6.5.0"),sQuery(id+"F0.wireOp",EDGE,"E6.5.1"),sQuery(id+"F0.wireOp",EDGE,"E6.5.2"),sQuery(id+"F0.wireOp",EDGE,"E6.5.3"),sQuery(id+"F0.wireOp",EDGE,"E6.5.4"),sQuery(id+"F0.wireOp",EDGE,"E6.6.0"),sQuery(id+"F0.wireOp",EDGE,"E6.6.1"),sQuery(id+"F0.wireOp",EDGE,"E6.6.2"),sQuery(id+"F0.wireOp",EDGE,"E6.6.3"),sQuery(id+"F0.wireOp",EDGE,"E6.6.4"),sQuery(id+"F0.wireOp",EDGE,"E6.7.0"),sQuery(id+"F0.wireOp",EDGE,"E6.7.1"),sQuery(id+"F0.wireOp",EDGE,"E6.7.2"),sQuery(id+"F0.wireOp",EDGE,"E6.7.3"),sQuery(id+"F0.wireOp",EDGE,"E6.7.4"),sQuery(id+"F0.wireOp",EDGE,"E6.8.0"),sQuery(id+"F0.wireOp",EDGE,"E6.8.1"),sQuery(id+"F0.wireOp",EDGE,"E6.8.2"),sQuery(id+"F0.wireOp",EDGE,"E6.8.3"),sQuery(id+"F0.wireOp",EDGE,"E6.8.4"),sQuery(id+"F0.wireOp",EDGE,"E6.9.0"),sQuery(id+"F0.wireOp",EDGE,"E6.9.1"),sQuery(id+"F0.wireOp",EDGE,"E6.9.2"),sQuery(id+"F0.wireOp",EDGE,"E6.9.3"),sQuery(id+"F0.wireOp",EDGE,"E6.9.4"),sQuery(id+"F0.wireOp",EDGE,"E6.10.0"),sQuery(id+"F0.wireOp",EDGE,"E6.10.1"),sQuery(id+"F0.wireOp",EDGE,"E6.10.2"),sQuery(id+"F0.wireOp",EDGE,"E6.10.3"),sQuery(id+"F0.wireOp",EDGE,"E6.10.4"),sQuery(id+"F0.wireOp",EDGE,"E6.11.0"),sQuery(id+"F0.wireOp",EDGE,"E6.11.1"),sQuery(id+"F0.wireOp",EDGE,"E6.11.2"),sQuery(id+"F0.wireOp",EDGE,"E6.11.3"),sQuery(id+"F0.wireOp",EDGE,"E6.11.4"),sQuery(id+"F0.wireOp",EDGE,"E6.12.0"),sQuery(id+"F0.wireOp",EDGE,"E6.12.1"),sQuery(id+"F0.wireOp",EDGE,"E6.12.2"),sQuery(id+"F0.wireOp",EDGE,"E6.12.3"),sQuery(id+"F0.wireOp",EDGE,"E6.12.4"),sQuery(id+"F0.wireOp",EDGE,"E6.13.0"),sQuery(id+"F0.wireOp",EDGE,"E6.13.1"),sQuery(id+"F0.wireOp",EDGE,"E6.13.2"),sQuery(id+"F0.wireOp",EDGE,"E6.13.3"),sQuery(id+"F0.wireOp",EDGE,"E6.13.4"),sQuery(id+"F0.wireOp",EDGE,"E6.14.0"),sQuery(id+"F0.wireOp",EDGE,"E6.14.1"),sQuery(id+"F0.wireOp",EDGE,"E6.14.2"),sQuery(id+"F0.wireOp",EDGE,"E6.14.3"),sQuery(id+"F0.wireOp",EDGE,"E6.14.4"),sQuery(id+"F0.wireOp",EDGE,"E6.15.0"),sQuery(id+"F0.wireOp",EDGE,"E6.15.1"),sQuery(id+"F0.wireOp",EDGE,"E6.15.2"),sQuery(id+"F0.wireOp",EDGE,"E6.15.3"),sQuery(id+"F0.wireOp",EDGE,"E6.15.4"),sQuery(id+"F0.wireOp",EDGE,"E6.16.0"),sQuery(id+"F0.wireOp",EDGE,"E6.16.1"),sQuery(id+"F0.wireOp",EDGE,"E6.16.2"),sQuery(id+"F0.wireOp",EDGE,"E6.16.3"),sQuery(id+"F0.wireOp",EDGE,"E6.16.4"),sQuery(id+"F0.wireOp",EDGE,"E6.17.0"),sQuery(id+"F0.wireOp",EDGE,"E6.17.1"),sQuery(id+"F0.wireOp",EDGE,"E6.17.2"),sQuery(id+"F0.wireOp",EDGE,"E6.17.3"),sQuery(id+"F0.wireOp",EDGE,"E6.17.4"),sQuery(id+"F0.wireOp",EDGE,"E6.18.0"),sQuery(id+"F0.wireOp",EDGE,"E6.18.1"),sQuery(id+"F0.wireOp",EDGE,"E6.18.2"),sQuery(id+"F0.wireOp",EDGE,"E6.18.3"),sQuery(id+"F0.wireOp",EDGE,"E6.18.4"),sQuery(id+"F0.wireOp",EDGE,"E6.19.0"),sQuery(id+"F0.wireOp",EDGE,"E6.19.1"),sQuery(id+"F0.wireOp",EDGE,"E6.19.2"),sQuery(id+"F0.wireOp",EDGE,"E6.19.3"),sQuery(id+"F0.wireOp",EDGE,"E6.19.4"),sQuery(id+"F0.wireOp",EDGE,"E6.20.0"),sQuery(id+"F0.wireOp",EDGE,"E6.20.1"),sQuery(id+"F0.wireOp",EDGE,"E6.20.2"),sQuery(id+"F0.wireOp",EDGE,"E6.20.3"),sQuery(id+"F0.wireOp",EDGE,"E6.20.4"),sQuery(id+"F0.wireOp",EDGE,"E6.21.0"),sQuery(id+"F0.wireOp",EDGE,"E6.21.1"),sQuery(id+"F0.wireOp",EDGE,"E6.21.2"),sQuery(id+"F0.wireOp",EDGE,"E6.21.3"),sQuery(id+"F0.wireOp",EDGE,"E6.21.4"),sQuery(id+"F0.wireOp",EDGE,"E6.22.0"),sQuery(id+"F0.wireOp",EDGE,"E6.22.1"),sQuery(id+"F0.wireOp",EDGE,"E6.22.2"),sQuery(id+"F0.wireOp",EDGE,"E6.22.3"),sQuery(id+"F0.wireOp",EDGE,"E6.22.4"),sQuery(id+"F0.wireOp",EDGE,"E6.23.0"),sQuery(id+"F0.wireOp",EDGE,"E6.23.1"),sQuery(id+"F0.wireOp",EDGE,"E6.23.2"),sQuery(id+"F0.wireOp",EDGE,"E6.23.3"),sQuery(id+"F0.wireOp",EDGE,"E6.23.4"),sQuery(id+"F0.wireOp",EDGE,"E6.24.0"),sQuery(id+"F0.wireOp",EDGE,"E6.24.1"),sQuery(id+"F0.wireOp",EDGE,"E6.24.2"),sQuery(id+"F0.wireOp",EDGE,"E6.24.3"),sQuery(id+"F0.wireOp",EDGE,"E6.24.4"),sQuery(id+"F0.wireOp",EDGE,"E6.25.0"),sQuery(id+"F0.wireOp",EDGE,"E6.25.1"),sQuery(id+"F0.wireOp",EDGE,"E6.25.2"),sQuery(id+"F0.wireOp",EDGE,"E6.25.3"),sQuery(id+"F0.wireOp",EDGE,"E6.25.4"),sQuery(id+"F0.wireOp",EDGE,"E6.26.0"),sQuery(id+"F0.wireOp",EDGE,"E6.26.1"),sQuery(id+"F0.wireOp",EDGE,"E6.26.2"),sQuery(id+"F0.wireOp",EDGE,"E6.26.3"),sQuery(id+"F0.wireOp",EDGE,"E6.26.4"),sQuery(id+"F0.wireOp",EDGE,"E6.27.0"),sQuery(id+"F0.wireOp",EDGE,"E6.27.1"),sQuery(id+"F0.wireOp",EDGE,"E6.27.2"),sQuery(id+"F0.wireOp",EDGE,"E6.27.3"),sQuery(id+"F0.wireOp",EDGE,"E6.27.4"),sQuery(id+"F0.wireOp",EDGE,"E6.28.0"),sQuery(id+"F0.wireOp",EDGE,"E6.28.1"),sQuery(id+"F0.wireOp",EDGE,"E6.28.2"),sQuery(id+"F0.wireOp",EDGE,"E6.28.3"),sQuery(id+"F0.wireOp",EDGE,"E6.28.4"),sQuery(id+"F0.wireOp",EDGE,"E6.29.0"),sQuery(id+"F0.wireOp",EDGE,"E6.29.1"),sQuery(id+"F0.wireOp",EDGE,"E6.29.2"),sQuery(id+"F0.wireOp",EDGE,"E6.29.3"),sQuery(id+"F0.wireOp",EDGE,"E6.29.4"),sQuery(id+"F0.wireOp",EDGE,"E6.30.0"),sQuery(id+"F0.wireOp",EDGE,"E6.30.1"),sQuery(id+"F0.wireOp",EDGE,"E6.30.2"),sQuery(id+"F0.wireOp",EDGE,"E6.30.3"),sQuery(id+"F0.wireOp",EDGE,"E6.30.4"),sQuery(id+"F0.wireOp",EDGE,"E6.31.0"),sQuery(id+"F0.wireOp",EDGE,"E6.31.1"),sQuery(id+"F0.wireOp",EDGE,"E6.31.2"),sQuery(id+"F0.wireOp",EDGE,"E6.31.3"),sQuery(id+"F0.wireOp",EDGE,"E6.31.4")])],"isStart":false});
            var sketch = newSketch(context, id + "F4", { "sketchPlane" : qUnion([Q0])});
            skCircle(sketch, "E8", {"center": v(0, 0) * mm, "radius": 4.37 * mm});
            skArc(sketch, "E9", {"start": v(2.13, 7.65) * mm, "mid": v(1.56, 7.8) * mm, "end": v(0.98, 7.88) * mm});
            skArc(sketch, "E10", {"start": v(2.45, 5.87) * mm, "mid": v(2.06, 4.88) * mm, "end": v(2.1, 3.83) * mm});
            skArc(sketch, "E11", {"start": v(-0.47, 4.34) * mm, "mid": v(-0.02, 5.3) * mm, "end": v(0, 6.36) * mm});
            skArc(sketch, "E12.trimOffspring", {"start": v(2.45, 5.87) * mm, "mid": v(2.46, 6.79) * mm, "end": v(2.13, 7.65) * mm});
            skArc(sketch, "E13.trimOffspring", {"start": v(0.98, 7.88) * mm, "mid": v(0.35, 7.21) * mm, "end": v(0, 6.36) * mm});
            skArc(sketch, "E14.1.0", {"start": v(-3.9, 6.92) * mm, "mid": v(-4.4, 6.61) * mm, "end": v(-4.88, 6.27) * mm});
            skArc(sketch, "E14.1.1", {"start": v(-4.88, 6.27) * mm, "mid": v(-4.86, 5.34) * mm, "end": v(-4.5, 4.5) * mm});
            skArc(sketch, "E14.1.2", {"start": v(-2.42, 5.88) * mm, "mid": v(-3.06, 6.54) * mm, "end": v(-3.9, 6.92) * mm});
            skArc(sketch, "E14.1.3", {"start": v(-2.42, 5.88) * mm, "mid": v(-2, 4.9) * mm, "end": v(-1.22, 4.2) * mm});
            skArc(sketch, "E14.1.4", {"start": v(-3.4, 2.74) * mm, "mid": v(-3.76, 3.74) * mm, "end": v(-4.5, 4.5) * mm});
            skArc(sketch, "E14.2.0", {"start": v(-7.65, 2.13) * mm, "mid": v(-7.8, 1.56) * mm, "end": v(-7.88, 0.98) * mm});
            skArc(sketch, "E14.2.1", {"start": v(-7.88, 0.98) * mm, "mid": v(-7.21, 0.35) * mm, "end": v(-6.36, 0) * mm});
            skArc(sketch, "E14.2.2", {"start": v(-5.87, 2.45) * mm, "mid": v(-6.79, 2.46) * mm, "end": v(-7.65, 2.13) * mm});
            skArc(sketch, "E14.2.3", {"start": v(-5.87, 2.45) * mm, "mid": v(-4.88, 2.06) * mm, "end": v(-3.83, 2.1) * mm});
            skArc(sketch, "E14.2.4", {"start": v(-4.34, -0.47) * mm, "mid": v(-5.3, -0.02) * mm, "end": v(-6.36, 0) * mm});
            skArc(sketch, "E14.3.0", {"start": v(-6.92, -3.9) * mm, "mid": v(-6.61, -4.4) * mm, "end": v(-6.27, -4.88) * mm});
            skArc(sketch, "E14.3.1", {"start": v(-6.27, -4.88) * mm, "mid": v(-5.34, -4.86) * mm, "end": v(-4.5, -4.5) * mm});
            skArc(sketch, "E14.3.2", {"start": v(-5.88, -2.42) * mm, "mid": v(-6.54, -3.06) * mm, "end": v(-6.92, -3.9) * mm});
            skArc(sketch, "E14.3.3", {"start": v(-5.88, -2.42) * mm, "mid": v(-4.9, -2) * mm, "end": v(-4.2, -1.22) * mm});
            skArc(sketch, "E14.3.4", {"start": v(-2.74, -3.4) * mm, "mid": v(-3.74, -3.76) * mm, "end": v(-4.5, -4.5) * mm});
            skArc(sketch, "E14.4.0", {"start": v(-2.13, -7.65) * mm, "mid": v(-1.56, -7.8) * mm, "end": v(-0.98, -7.88) * mm});
            skArc(sketch, "E14.4.1", {"start": v(-0.98, -7.88) * mm, "mid": v(-0.35, -7.21) * mm, "end": v(0, -6.36) * mm});
            skArc(sketch, "E14.4.2", {"start": v(-2.45, -5.87) * mm, "mid": v(-2.46, -6.79) * mm, "end": v(-2.13, -7.65) * mm});
            skArc(sketch, "E14.4.3", {"start": v(-2.45, -5.87) * mm, "mid": v(-2.06, -4.88) * mm, "end": v(-2.1, -3.83) * mm});
            skArc(sketch, "E14.4.4", {"start": v(0.47, -4.34) * mm, "mid": v(0.02, -5.3) * mm, "end": v(0, -6.36) * mm});
            skArc(sketch, "E14.5.0", {"start": v(3.9, -6.92) * mm, "mid": v(4.4, -6.61) * mm, "end": v(4.88, -6.27) * mm});
            skArc(sketch, "E14.5.1", {"start": v(4.88, -6.27) * mm, "mid": v(4.86, -5.34) * mm, "end": v(4.5, -4.5) * mm});
            skArc(sketch, "E14.5.2", {"start": v(2.42, -5.88) * mm, "mid": v(3.06, -6.54) * mm, "end": v(3.9, -6.92) * mm});
            skArc(sketch, "E14.5.3", {"start": v(2.42, -5.88) * mm, "mid": v(2, -4.9) * mm, "end": v(1.22, -4.2) * mm});
            skArc(sketch, "E14.5.4", {"start": v(3.4, -2.74) * mm, "mid": v(3.76, -3.74) * mm, "end": v(4.5, -4.5) * mm});
            skArc(sketch, "E14.6.0", {"start": v(7.65, -2.13) * mm, "mid": v(7.8, -1.56) * mm, "end": v(7.88, -0.98) * mm});
            skArc(sketch, "E14.6.1", {"start": v(7.88, -0.98) * mm, "mid": v(7.21, -0.35) * mm, "end": v(6.36, 0) * mm});
            skArc(sketch, "E14.6.2", {"start": v(5.87, -2.45) * mm, "mid": v(6.79, -2.46) * mm, "end": v(7.65, -2.13) * mm});
            skArc(sketch, "E14.6.3", {"start": v(5.87, -2.45) * mm, "mid": v(4.88, -2.06) * mm, "end": v(3.83, -2.1) * mm});
            skArc(sketch, "E14.6.4", {"start": v(4.34, 0.47) * mm, "mid": v(5.3, 0.02) * mm, "end": v(6.36, 0) * mm});
            skArc(sketch, "E14.7.0", {"start": v(6.92, 3.9) * mm, "mid": v(6.61, 4.4) * mm, "end": v(6.27, 4.88) * mm});
            skArc(sketch, "E14.7.1", {"start": v(6.27, 4.88) * mm, "mid": v(5.34, 4.86) * mm, "end": v(4.5, 4.5) * mm});
            skArc(sketch, "E14.7.2", {"start": v(5.88, 2.42) * mm, "mid": v(6.54, 3.06) * mm, "end": v(6.92, 3.9) * mm});
            skArc(sketch, "E14.7.3", {"start": v(5.88, 2.42) * mm, "mid": v(4.9, 2) * mm, "end": v(4.2, 1.22) * mm});
            skArc(sketch, "E14.7.4", {"start": v(2.74, 3.4) * mm, "mid": v(3.74, 3.76) * mm, "end": v(4.5, 4.5) * mm});
            skSolve(sketch);
        }
        {
            var Q0;
            Q0=makeQuery(id+"F4.imprint","IMPRINT",FACE,{"disambiguationData":[TD([[makeQuery(id+"F4.imprint","IMPRINT",EDGE,{"derivedFrom":sQuery(id+"F4.wireOp",EDGE,"E14.1.0")}),1.0]])]});
            var Q1;
            Q1=makeQuery(id+"F4.imprint","IMPRINT",FACE,{"disambiguationData":[TD([[makeQuery(id+"F4.imprint","IMPRINT",EDGE,{"derivedFrom":sQuery(id+"F4.wireOp",EDGE,"E9")}),1.0]])]});
            var Q2;
            Q2=makeQuery(id+"F4.imprint","IMPRINT",FACE,{"disambiguationData":[TD([[makeQuery(id+"F4.imprint","IMPRINT",EDGE,{"derivedFrom":makeQuery(id+"F3.boolean.opBoolean","COPY",EDGE,{"derivedFrom":makeQuery(id+"F3.opExtrude","CAP_EDGE",EDGE,{"disambiguationData":[OSD([sQuery(id+"F2.wireOp",EDGE,"E7")])],"isStart":true})})}),-1.0]])]});
            var Q3;
            Q3=makeQuery(id+"F4.imprint","IMPRINT",FACE,{"disambiguationData":[TD([[makeQuery(id+"F4.imprint","IMPRINT",EDGE,{"derivedFrom":sQuery(id+"F4.wireOp",EDGE,"E14.7.0")}),1.0]])]});
            var Q4;
            Q4=makeQuery(id+"F4.imprint","IMPRINT",FACE,{"disambiguationData":[TD([[makeQuery(id+"F4.imprint","IMPRINT",EDGE,{"derivedFrom":sQuery(id+"F4.wireOp",EDGE,"E14.6.0")}),1.0]])]});
            var Q5;
            Q5=makeQuery(id+"F4.imprint","IMPRINT",FACE,{"disambiguationData":[TD([[makeQuery(id+"F4.imprint","IMPRINT",EDGE,{"derivedFrom":sQuery(id+"F4.wireOp",EDGE,"E14.5.0")}),1.0]])]});
            var Q6;
            Q6=makeQuery(id+"F4.imprint","IMPRINT",FACE,{"disambiguationData":[TD([[makeQuery(id+"F4.imprint","IMPRINT",EDGE,{"derivedFrom":sQuery(id+"F4.wireOp",EDGE,"E14.4.0")}),1.0]])]});
            var Q7;
            Q7=makeQuery(id+"F4.imprint","IMPRINT",FACE,{"disambiguationData":[TD([[makeQuery(id+"F4.imprint","IMPRINT",EDGE,{"derivedFrom":sQuery(id+"F4.wireOp",EDGE,"E14.3.0")}),1.0]])]});
            var Q8;
            Q8=makeQuery(id+"F4.imprint","IMPRINT",FACE,{"disambiguationData":[TD([[makeQuery(id+"F4.imprint","IMPRINT",EDGE,{"derivedFrom":sQuery(id+"F4.wireOp",EDGE,"E14.2.0")}),1.0]])]});
            extrude(context, id + "F5", {"entities" : qUnion([Q0, Q1, Q2, Q3, Q4, Q5, Q6, Q7, Q8]), "operationType" : NewBodyOperationType.ADD, "depth" : 6 * mm, "offsetDistance" : 25 * mm});
        }
    });
